# Revit family: SVX-SIENNA-Modular_Lounge_Seating
name_source: partatom
category: Furniture
revit_build: Autodesk Revit 2014 (Build: 20140709_2115(x64)
units: mm (PartAtom-declared; Revit-internal decimal feet)

## types (6) — shared parameters
Assembly Code = E2020200
Glides = VIA-UHMW, Black
Keynote = 12500
Low Emitting Finish = Yes
Low Emitting Material = Yes
Manufacturer = Via Seating
Salvage or Reuse = Yes
Seat Width = 20 1/2"
Type Comments = SIENNA
URL = www.viaseating.com
Upholstery = VIA-Linen - Beige
zero-valued in all types: Percentage of Recycled Content

## per-type parameters (varying)
| type | # of Seat | Arm | Description | Model | Seat Array Dist | Single Chair | Width |
| 95-RSL - Single Seat With Club Arms | 2 | Arm_Club | Single Seat With Club Arms | 95-RSL | 0" | Yes | 30 3/4" |
| 95-USSU - Double Seats With Universal Arms | 2 | Arm_Universal | Double Seats With Universal Arms | 95-USSU | 20 3/4" | No | 51 1/2" |
| 95-RSSSL - Triple Seats With Club Arms | 3 | Arm_Club | Triple Seats With Club Arms | 95-RSSSL | 20 3/4" | No | 72 1/4" |
| 95-USU - Single Seat With Universal Arms | 2 | Arm_Universal | Single Seat With Universal Arms | 95-USU | 0" | Yes | 30 3/4" |
| 95-USSSU - Triple Seats With Universal Arms | 3 | Arm_Universal | Triple Seats With Universal Arms | 95-USSSU | 20 3/4" | No | 72 1/4" |
| 95-RSSL - Double Seats With Club Arms | 2 | Arm_Club | Double Seats With Club Arms | 95-USSU | 20 3/4" | No | 51 1/2" |

## geometry (parser evidence)
native form markers: Sweep x10
no freeform markers — native parametric forms only
